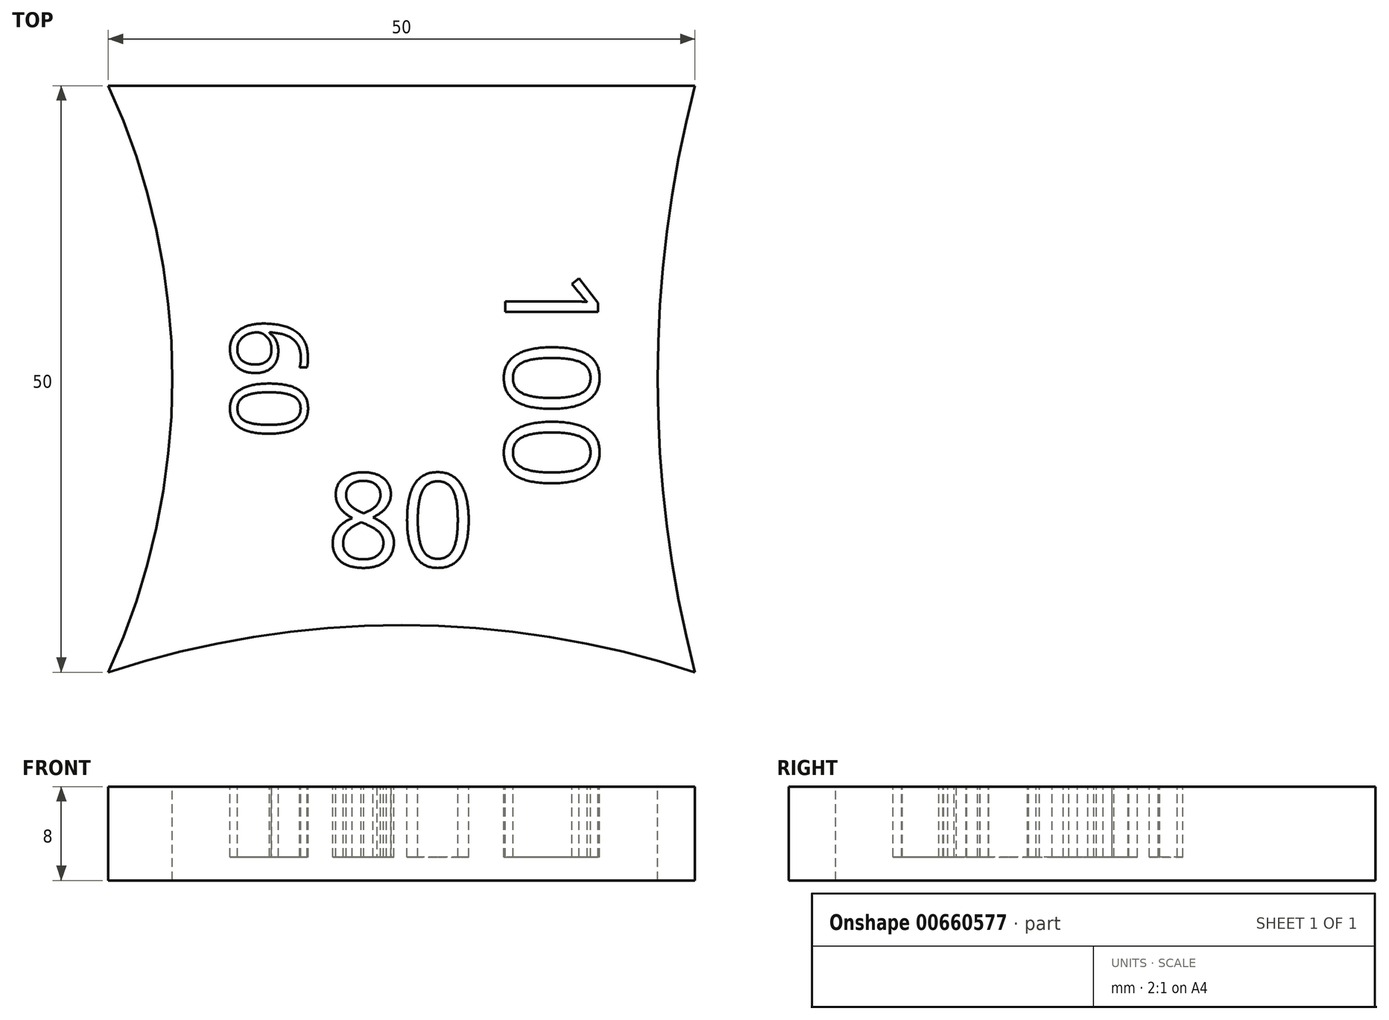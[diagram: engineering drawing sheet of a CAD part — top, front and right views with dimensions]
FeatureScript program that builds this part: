
annotation { "Feature Type Name" : "Feature", "Feature Type Description" : "" }
export const myFeature = defineFeature(function(context is Context, id is Id, definition is map)
    precondition{}
    {
        {
            var Q0;
            Q0=qCreatedBy(makeId("Top.planeOp"),FACE);
            var sketch = newSketch(context, id + "F0", { "sketchPlane" : qUnion([Q0])});
            skLineSegment(sketch, "E0.bottom", {"start": v(0, 0) * mm, "end": v(50, 0) * mm});
            skLineSegment(sketch, "E0.top", {"start": v(0, -50) * mm, "end": v(50, -50) * mm});
            skLineSegment(sketch, "E0.left", {"start": v(0, 0) * mm, "end": v(0, -50) * mm});
            skLineSegment(sketch, "E0.right", {"start": v(50, 0) * mm, "end": v(50, -50) * mm});
            skSolve(sketch);
        }
        {
            var Q0;
            Q0=makeQuery(id+"F0.imprint","IMPRINT",FACE,{"disambiguationData":[TD([[makeQuery(id+"F0.imprint","IMPRINT",EDGE,{"derivedFrom":sQuery(id+"F0.wireOp",EDGE,"E0.bottom")}),-1.0]])]});
            extrude(context, id + "F1", {"entities" : qUnion([Q0]), "depth" : 8 * mm, "offsetDistance" : 25 * mm});
        }
        {
            var Q0;
            Q0=makeQuery(id+"F1.opExtrude","CAP_FACE",FACE,{"disambiguationData":[OSD([sQuery(id+"F0.wireOp",EDGE,"E0.bottom"),sQuery(id+"F0.wireOp",EDGE,"E0.top"),sQuery(id+"F0.wireOp",EDGE,"E0.left"),sQuery(id+"F0.wireOp",EDGE,"E0.right")])],"isStart":false});
            var sketch = newSketch(context, id + "F2", { "sketchPlane" : qUnion([Q0])});
            skArc(sketch, "E1", {"start": v(0, -50) * mm, "mid": v(5.46, -25) * mm, "end": v(0, 0) * mm});
            skArc(sketch, "E2", {"start": v(50, -50) * mm, "mid": v(25, -46) * mm, "end": v(0, -50) * mm});
            skArc(sketch, "E3", {"start": v(50, 0) * mm, "mid": v(46.82, -25) * mm, "end": v(50, -50) * mm});
            skText(sketch, "E4", { "text": "100", "fontName": "OpenSans-Regular.ttf"});
            skText(sketch, "E5", { "text": "80", "fontName": "OpenSans-Regular.ttf"});
            skText(sketch, "E6", { "text": "60", "fontName": "OpenSans-Regular.ttf"});
            skLineSegment(sketch, "E7", {"start": v(0, 0) * mm, "end": v(-44.37, -1.76) * mm});
            skLineSegment(sketch, "E8", {"start": v(-44.37, -1.76) * mm, "end": v(-30.66, -60.31) * mm});
            skLineSegment(sketch, "E9", {"start": v(-30.66, -60.31) * mm, "end": v(36.1, -65.05) * mm});
            skLineSegment(sketch, "E10", {"start": v(36.1, -65.05) * mm, "end": v(101.63, -49.85) * mm});
            skLineSegment(sketch, "E11", {"start": v(101.63, -49.85) * mm, "end": v(67, -23.44) * mm});
            skLineSegment(sketch, "E12", {"start": v(67, -23.44) * mm, "end": v(50, 0) * mm});
            const initialGuessF2  = {"E4": [0.03382, -0.01539, 0, -1, 0.008], "E5": [0.01856, -0.041, 1, 0, 0.008], "E6": [0.01046, -0.01976, 0, -1, 0.00652]};
            skSetInitialGuess(sketch, initialGuessF2);
            skSolve(sketch);
        }
        {
            var Q0;
            Q0 = qSketchRegion(id + "F2", true);
            extrude(context, id + "F3", {"entities" : qUnion([Q0]), "operationType" : NewBodyOperationType.REMOVE, "oppositeDirection" : true, "depth" : 25 * mm, "offsetDistance" : 25 * mm});
        }
        {
            var Q0;
            {var subQ0=sQuery(id+"F0.wireOp",EDGE,"E0.bottom");Q0=makeQuery(id+"F3.boolean.opBoolean","SPLIT",FACE,{"disambiguationData":[TD([makeQuery(id+"F1.opExtrude","SWEPT_FACE",FACE,{"disambiguationData":[OSD([subQ0])]})])],"derivedFrom":makeQuery(id+"F1.opExtrude","CAP_FACE",FACE,{"disambiguationData":[OSD([subQ0,sQuery(id+"F0.wireOp",EDGE,"E0.top"),sQuery(id+"F0.wireOp",EDGE,"E0.left"),sQuery(id+"F0.wireOp",EDGE,"E0.right")])],"isStart":true})});}
            var sketch = newSketch(context, id + "F4", { "sketchPlane" : qUnion([Q0])});
            skLineSegment(sketch, "E13.bottom", {"start": v(8.28, 43.78) * mm, "end": v(44.75, 43.78) * mm});
            skLineSegment(sketch, "E13.top", {"start": v(8.28, 13.3) * mm, "end": v(44.75, 13.3) * mm});
            skLineSegment(sketch, "E13.left", {"start": v(8.28, 43.78) * mm, "end": v(8.28, 13.3) * mm});
            skLineSegment(sketch, "E13.right", {"start": v(44.75, 43.78) * mm, "end": v(44.75, 13.3) * mm});
            skSolve(sketch);
        }
        {
            var Q0;
            Q0 = qSketchRegion(id + "F4", true);
            extrude(context, id + "F5", {"entities" : qUnion([Q0]), "operationType" : NewBodyOperationType.ADD, "oppositeDirection" : true, "depth" : 2 * mm, "offsetDistance" : 25 * mm});
        }
    });
